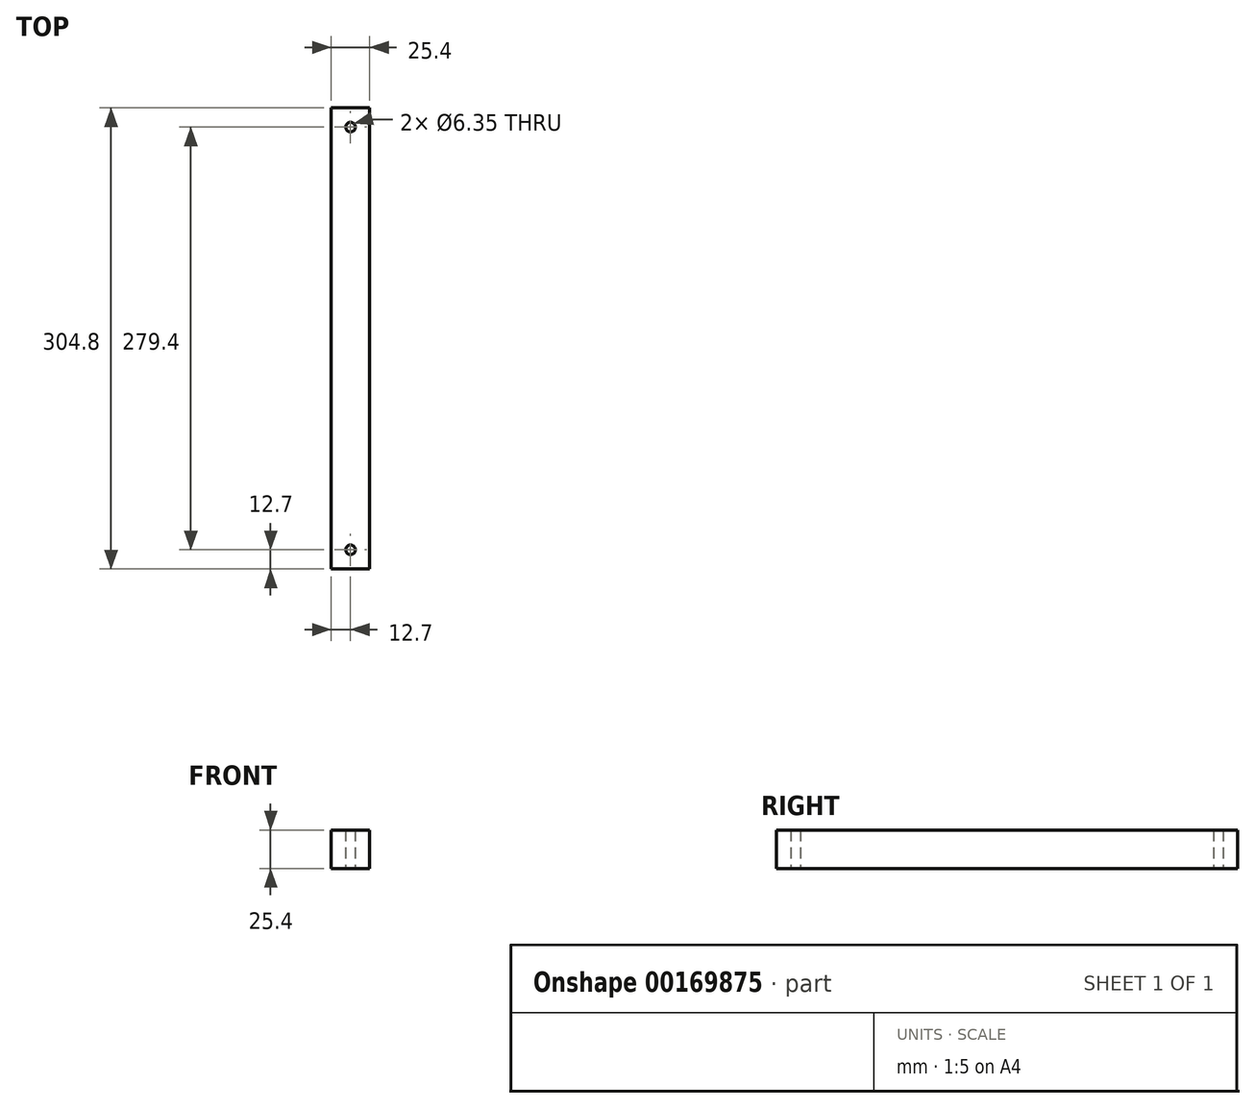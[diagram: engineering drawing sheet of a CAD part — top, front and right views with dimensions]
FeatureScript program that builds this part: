
annotation { "Feature Type Name" : "Feature", "Feature Type Description" : "" }
export const myFeature = defineFeature(function(context is Context, id is Id, definition is map)
    precondition{}
    {
        {
            var Q0;
            Q0=qCreatedBy(makeId("Top.planeOp"),FACE);
            var sketch = newSketch(context, id + "F0", { "sketchPlane" : qUnion([Q0])});
            skLineSegment(sketch, "E0", {"start": v(0, 0) * mm, "end": v(-25.4, 0) * mm});
            skLineSegment(sketch, "E1", {"start": v(-25.4, 0) * mm, "end": v(-25.4, -304.8) * mm});
            skLineSegment(sketch, "E2", {"start": v(-25.4, -304.8) * mm, "end": v(0, -304.8) * mm});
            skLineSegment(sketch, "E3", {"start": v(0, -304.8) * mm, "end": v(0, 0) * mm});
            skLineSegment(sketch, "E4", {"start": v(-12.7, 0) * mm, "end": v(-12.7, -12.7) * mm, "construction": true});
            skLineSegment(sketch, "E5", {"start": v(-12.7, -12.7) * mm, "end": v(-12.7, -304.8) * mm, "construction": true});
            skLineSegment(sketch, "E6", {"start": v(-25.4, -12.7) * mm, "end": v(-12.7, -12.7) * mm, "construction": true});
            skLineSegment(sketch, "E7", {"start": v(-12.7, -12.7) * mm, "end": v(0, -12.7) * mm, "construction": true});
            skLineSegment(sketch, "E8", {"start": v(-25.4, -152.4) * mm, "end": v(-12.7, -152.4) * mm, "construction": true});
            skCircle(sketch, "E9", {"center": v(-12.7, -12.7) * mm, "radius": 3.18 * mm});
            skCircle(sketch, "E10.MirrorC", {"center": v(-12.7, -292.1) * mm, "radius": 3.18 * mm});
            skSolve(sketch);
        }
        {
            var Q0;
            Q0 = qSketchRegion(id + "F0", true);
            extrude(context, id + "F1", {"entities" : qUnion([Q0]), "depth" : 25.4 * mm});
        }
    });
